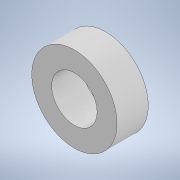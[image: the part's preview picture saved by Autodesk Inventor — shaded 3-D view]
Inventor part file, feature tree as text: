
AUTODESK INVENTOR PART (.ipt)
format: ipt  version: 2021 (Build 250183000, 183)  size: 97,792 bytes
history: native  units: mm
features: extrude x1, sketch x1
ambient origin geometry x8: Origin, YZ Plane, XZ Plane, XY Plane, X Axis, Y Axis, Z Axis, Center Point
bodies: Solid1 (feature_tree)
feature tree (2):
  extrude  "Extrusion1"  Depth=5.5mm
  sketch  "Sketch1"  dims[d0=8.0mm d1=15.0mm d2=5.5mm d3=0.0mm]
